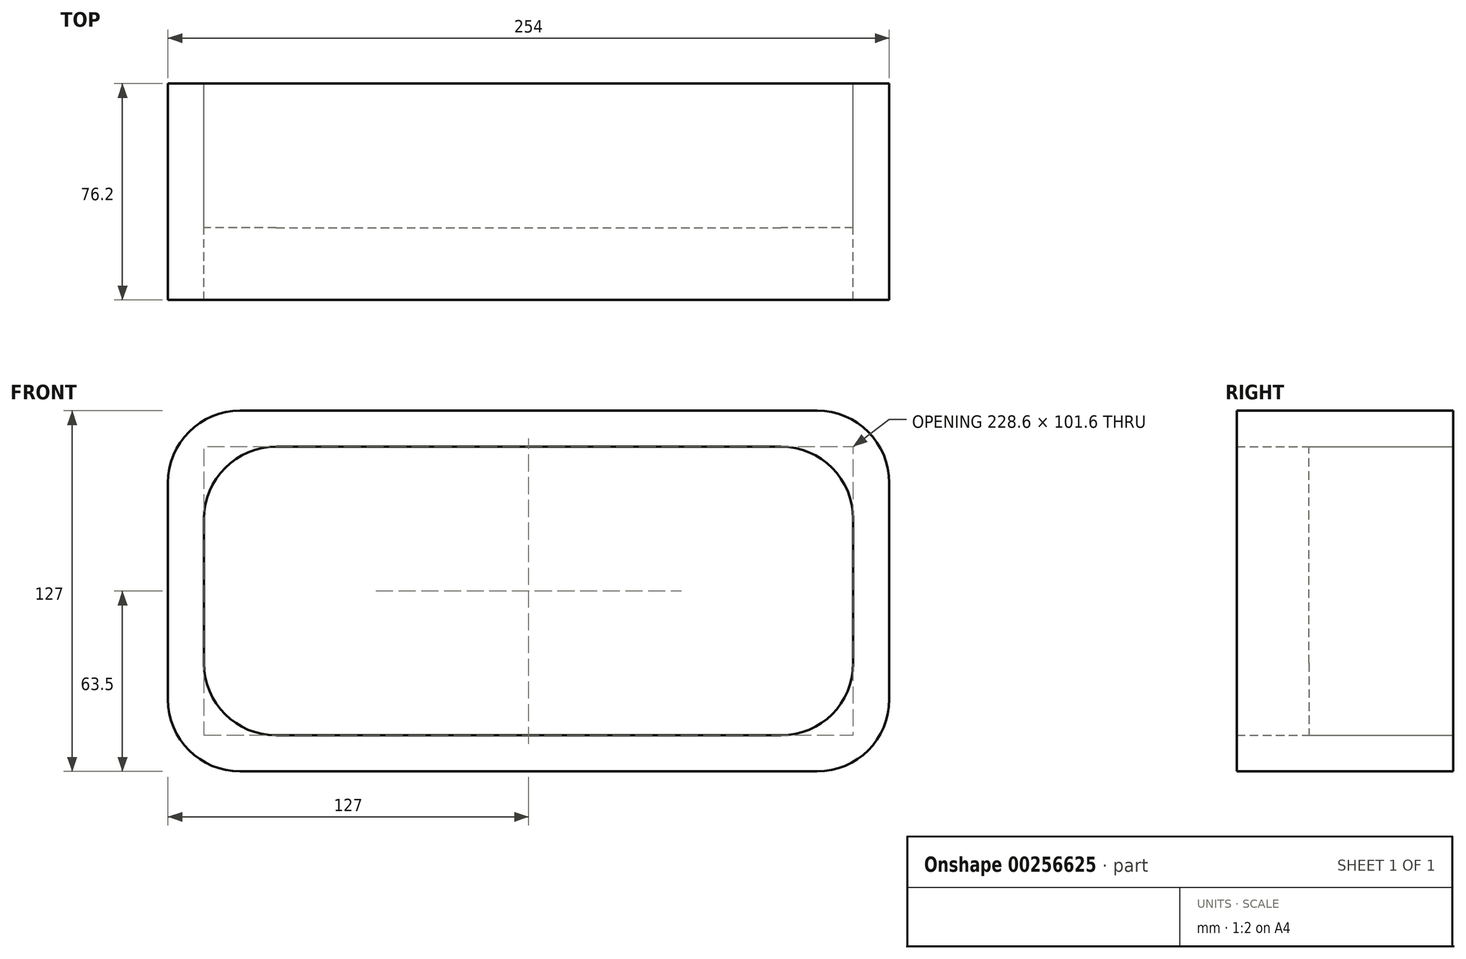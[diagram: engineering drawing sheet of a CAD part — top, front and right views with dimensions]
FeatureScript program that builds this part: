
annotation { "Feature Type Name" : "Feature", "Feature Type Description" : "" }
export const myFeature = defineFeature(function(context is Context, id is Id, definition is map)
    precondition{}
    {
        {
            var Q0;
            Q0=qCreatedBy(makeId("Front.planeOp"),FACE);
            var sketch = newSketch(context, id + "F0", { "sketchPlane" : qUnion([Q0])});
            skLineSegment(sketch, "E0.bottom", {"start": v(-101.6, -63.5) * mm, "end": v(101.6, -63.5) * mm});
            skLineSegment(sketch, "E0.top", {"start": v(-101.6, 63.5) * mm, "end": v(101.6, 63.5) * mm});
            skLineSegment(sketch, "E0.left", {"start": v(-127, -38.1) * mm, "end": v(-127, 38.1) * mm});
            skLineSegment(sketch, "E0.right", {"start": v(127, -38.1) * mm, "end": v(127, 38.1) * mm});
            skPoint(sketch, "E0.middle", {"position": v(0, 0) * mm});
            skPoint(sketch, "E1.visualSharp", {"position": v(-127, 63.5) * mm});
            skArc(sketch, "E1.filletArc", {"start": v(-101.6, 63.5) * mm, "mid": v(-119.56, 56.06) * mm, "end": v(-127, 38.1) * mm});
            skPoint(sketch, "E2.visualSharp", {"position": v(127, 63.5) * mm});
            skArc(sketch, "E2.filletArc", {"start": v(127, 38.1) * mm, "mid": v(119.56, 56.06) * mm, "end": v(101.6, 63.5) * mm});
            skPoint(sketch, "E3.visualSharp", {"position": v(-127, -63.5) * mm});
            skArc(sketch, "E3.filletArc", {"start": v(-127, -38.1) * mm, "mid": v(-119.56, -56.06) * mm, "end": v(-101.6, -63.5) * mm});
            skPoint(sketch, "E4.visualSharp", {"position": v(127, -63.5) * mm});
            skArc(sketch, "E4.filletArc", {"start": v(101.6, -63.5) * mm, "mid": v(119.56, -56.06) * mm, "end": v(127, -38.1) * mm});
            skLineSegment(sketch, "E5.bottom", {"start": v(-88.9, -50.8) * mm, "end": v(88.9, -50.8) * mm});
            skLineSegment(sketch, "E5.top", {"start": v(-88.9, 50.8) * mm, "end": v(88.9, 50.8) * mm});
            skLineSegment(sketch, "E5.left", {"start": v(-114.3, -25.4) * mm, "end": v(-114.3, 25.4) * mm});
            skLineSegment(sketch, "E5.right", {"start": v(114.3, -25.4) * mm, "end": v(114.3, 25.4) * mm});
            skPoint(sketch, "E6.visualSharp", {"position": v(-114.3, 50.8) * mm});
            skArc(sketch, "E6.filletArc", {"start": v(-88.9, 50.8) * mm, "mid": v(-106.86, 43.36) * mm, "end": v(-114.3, 25.4) * mm});
            skPoint(sketch, "E7.visualSharp", {"position": v(114.3, 50.8) * mm});
            skArc(sketch, "E7.filletArc", {"start": v(114.3, 25.4) * mm, "mid": v(106.86, 43.36) * mm, "end": v(88.9, 50.8) * mm});
            skPoint(sketch, "E8.visualSharp", {"position": v(114.3, -50.8) * mm});
            skArc(sketch, "E8.filletArc", {"start": v(88.9, -50.8) * mm, "mid": v(106.86, -43.36) * mm, "end": v(114.3, -25.4) * mm});
            skPoint(sketch, "E9.visualSharp", {"position": v(-114.3, -50.8) * mm});
            skArc(sketch, "E9.filletArc", {"start": v(-114.3, -25.4) * mm, "mid": v(-106.86, -43.36) * mm, "end": v(-88.9, -50.8) * mm});
            skSolve(sketch);
        }
        {
            var Q0;
            Q0=makeQuery(id+"F0.imprint","IMPRINT",FACE,{"disambiguationData":[TD([[makeQuery(id+"F0.imprint","IMPRINT",EDGE,{"derivedFrom":sQuery(id+"F0.wireOp",EDGE,"E5.bottom")}),1.0]])]});
            extrude(context, id + "F1", {"entities" : qUnion([Q0]), "depth" : 50.8 * mm});
        }
        {
            var Q0;
            Q0=makeQuery(id+"F0.imprint","IMPRINT",FACE,{"disambiguationData":[TD([[makeQuery(id+"F0.imprint","IMPRINT",EDGE,{"derivedFrom":sQuery(id+"F0.wireOp",EDGE,"E0.bottom")}),1.0]])]});
            extrude(context, id + "F2", {"entities" : qUnion([Q0]), "depth" : 76.2 * mm});
        }
    });
